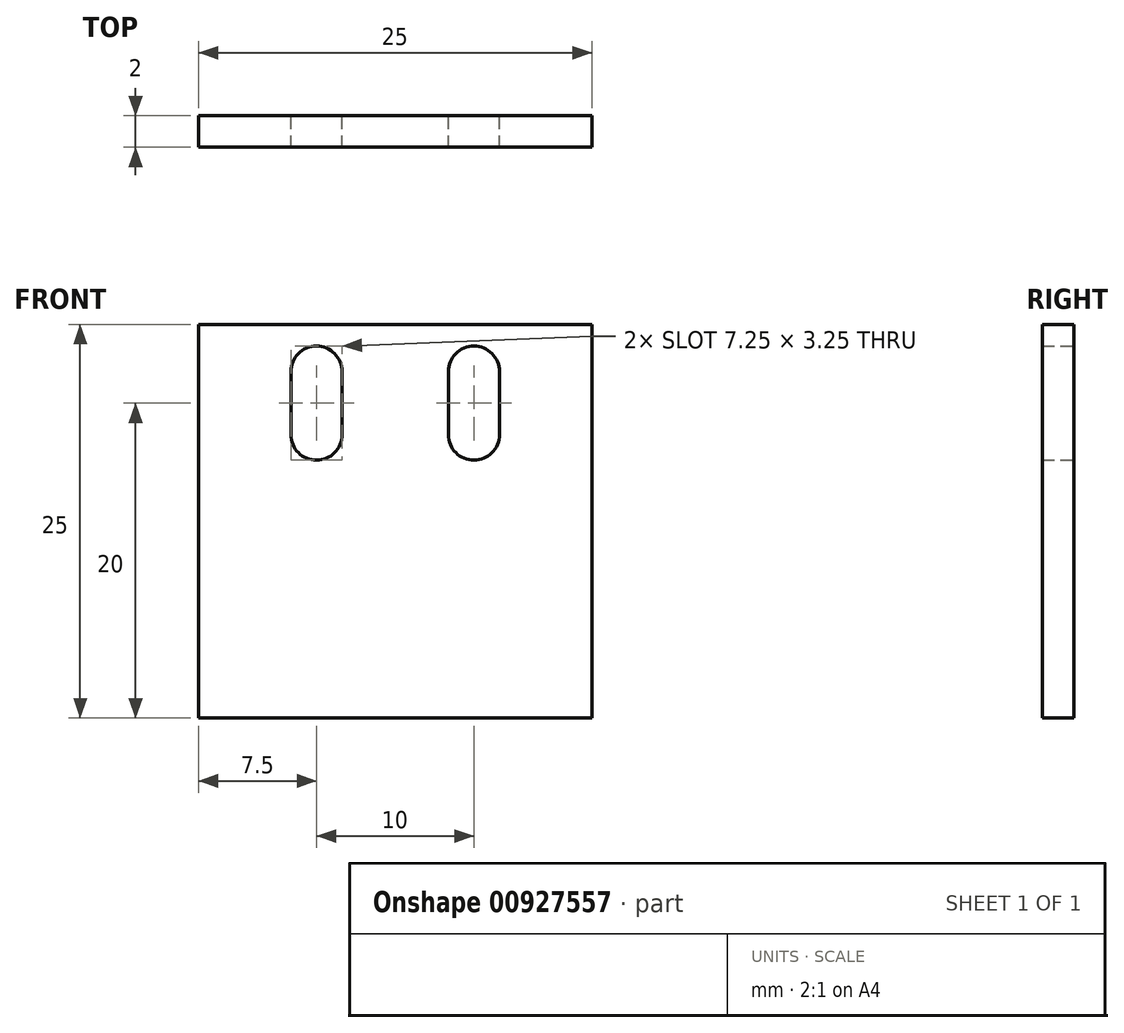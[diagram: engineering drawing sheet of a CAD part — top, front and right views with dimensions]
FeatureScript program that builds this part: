
annotation { "Feature Type Name" : "Feature", "Feature Type Description" : "" }
export const myFeature = defineFeature(function(context is Context, id is Id, definition is map)
    precondition{}
    {
        {
            var Q0;
            Q0=qCreatedBy(makeId("Right.planeOp"),FACE);
            var sketch = newSketch(context, id + "F0", { "sketchPlane" : qUnion([Q0])});
            skLineSegment(sketch, "E0", {"start": v(0, 0) * mm, "end": v(0, 10) * mm});
            skLineSegment(sketch, "E1", {"start": v(0, 0) * mm, "end": v(0, -15) * mm});
            skLineSegment(sketch, "E2.0", {"start": v(2, 2) * mm, "end": v(2, 10) * mm});
            skLineSegment(sketch, "E2.2", {"start": v(2, 2) * mm, "end": v(2, -15) * mm});
            skLineSegment(sketch, "E3", {"start": v(0, -15) * mm, "end": v(2, -15) * mm});
            skLineSegment(sketch, "E4", {"start": v(0, 10) * mm, "end": v(2, 10) * mm});
            skSolve(sketch);
        }
        {
            var Q0;
            Q0 = qSketchRegion(id + "F0", true);
            extrude(context, id + "F1", {"entities" : qUnion([Q0]), "depth" : 25 * mm, "offsetDistance" : 25 * mm});
        }
        {
            var Q0;
            Q0=makeQuery(id+"F1.opExtrude","SWEPT_FACE",FACE,{"disambiguationData":[OSD([sQuery(id+"F0.wireOp",EDGE,"E2.0")])]});
            var sketch = newSketch(context, id + "F2", { "sketchPlane" : qUnion([Q0])});
            skArc(sketch, "E5", {"start": v(-15.88, 7) * mm, "mid": v(-17.5, 8.62) * mm, "end": v(-19.13, 7) * mm});
            skArc(sketch, "E6", {"start": v(-5.88, 7) * mm, "mid": v(-7.5, 8.62) * mm, "end": v(-9.12, 7) * mm});
            skArc(sketch, "E7", {"start": v(-19.13, 3) * mm, "mid": v(-17.5, 1.37) * mm, "end": v(-15.88, 3) * mm});
            skArc(sketch, "E8", {"start": v(-9.13, 3) * mm, "mid": v(-7.5, 1.38) * mm, "end": v(-5.88, 3) * mm});
            skLineSegment(sketch, "E9", {"start": v(-19.13, 7) * mm, "end": v(-19.13, 3) * mm});
            skLineSegment(sketch, "E10", {"start": v(-15.88, 7) * mm, "end": v(-15.88, 3) * mm});
            skLineSegment(sketch, "E11", {"start": v(-9.12, 7) * mm, "end": v(-9.12, 3) * mm});
            skLineSegment(sketch, "E12", {"start": v(-5.87, 7) * mm, "end": v(-5.87, 3) * mm});
            skSolve(sketch);
        }
        {
            var Q0;
            Q0 = qSketchRegion(id + "F2", true);
            extrude(context, id + "F3", {"entities" : qUnion([Q0]), "operationType" : NewBodyOperationType.REMOVE, "oppositeDirection" : true, "depth" : 25 * mm, "offsetDistance" : 25 * mm});
        }
    });
